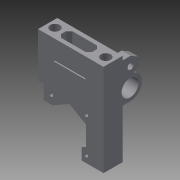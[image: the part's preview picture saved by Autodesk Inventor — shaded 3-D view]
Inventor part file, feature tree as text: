
AUTODESK INVENTOR PART (.ipt)
format: ipt  version: 2015 (Build 190159000, 159)  size: 260,608 bytes
history: native  units: mm
features: sketch x11, extrude x9, hole x3, chamfer x1
ambient origin geometry x8: Origin, YZ Plane, XZ Plane, XY Plane, X Axis, Y Axis, Z Axis, Center Point
bodies: Solid1 (feature_tree)
feature tree (24):
  extrude  "Extrusion1"  Depth=58.0mm
  extrude  "Extrusion2"  Depth=17.0mm
  sketch  "Sketch3"  dims[d5=38.0mm d6=27.75mm]
  extrude  "Extrusion4"  Depth=38.0mm
  extrude  "Extrusion5"  Depth=19.25mm TaperAngle=0.0deg
  extrude  "Extrusion6"  Depth=3.0mm
  extrude  "Extrusion7"  Depth=15.0mm
  extrude  "Extrusion9"  Depth=8.0mm
  hole  "Hole1"  [1 undecoded]
  hole  "Hole2"  [1 undecoded]
  chamfer  "Chamfer1"  Distance=1.0mm
  hole  "Hole3"  [1 undecoded]
  extrude  "Extrusion10"  Depth=10.0mm TaperAngle=0.0deg
  extrude  "Extrusion11"  Depth=10.0mm
  sketch  "Sketch1"  dims[d0=81.5mm d1=58.0mm]
  sketch  "Sketch2"  dims[d2=35.0mm d3=0.0mm d4=17.0mm]
  sketch  "Sketch4"  dims[d7=19.25mm d8=35.0mm d9=0.0mm]
  sketch  "Sketch5"  dims[d10=17.0mm d11=3.0mm]
  sketch  "Sketch6"  dims[d12=15.0mm d13=6.5mm]
  sketch  "Sketch7"  dims[d14=3.5mm d15=8.0mm]
  sketch  "Sketch8"  dims[d19=0.0mm d20=0.0mm d21=8.0mm]
  sketch  "Sketch9"  dims[d22=35.0mm d23=0.0mm d24=12.5mm]
  sketch  "Sketch12"  dims[d25=5.0mm]
  sketch  "Sketch13"  dims[d26=8.0mm d27=1.0mm d28=28.0mm d29=10.0mm d30=0.0mm d31=10.0mm d32=22.0mm d33=10.0mm d34=0.0mm d39=13.75mm d40=135.0deg d41=2.75mm d43=41.5mm d44=0.0mm d45=31.0mm d46=31.0mm d47=6.485mm d48=7.66mm d49=3.6mm d50=6.0mm d51=6.2mm d52=3.5mm d53=90.0deg d54=8.0mm d55=20.594885mm d56=45.0mm d57=8.5mm d58=6.5mm d59=8.5mm d60=6.0mm d61=3.023mm d62=3.5mm d63=14.3117mm d64=37.0mm d65=0.0mm d67=10.0mm d68=2.0mm d69=45.0deg d70=5.4mm d71=6.0mm d72=3.023mm d73=3.5mm d74=14.3117mm d75=41.5mm d76=0.0mm d77=3.5mm d78=7.794mm d79=5.0mm d80=0.0mm d81=1.0mm d82=1.675mm d83=5.0mm d84=0.0mm]
note: 3 required parameter values undecoded (feature->parameter linkage not recoverable at this tier; creation-order binding heuristic only, values carry confidence <= 0.55)
